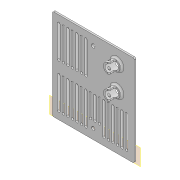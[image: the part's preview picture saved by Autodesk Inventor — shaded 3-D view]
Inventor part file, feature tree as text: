
AUTODESK INVENTOR PART (.ipt)
format: ipt  version: 2020 (Build 240168000, 168)  size: 380,928 bytes
history: native  units: mm
features: other x9, extrude x4, sketch x4, fillet x2
ambient origin geometry x8: Origin, YZ Plane, XZ Plane, XY Plane, X Axis, Y Axis, Z Axis, Center Point
bodies: Body1 (feature_tree)
feature tree (19):
  other  "Sólido1"
  other  "Plano de trabalho1"
  extrude  "Extrusão1"  Depth=0.5mm
  extrude  "Extrusão2"  Depth=1.0mm
  fillet  "Arredondamento1"  Radius=0.5mm
  extrude  "Extrusão3"  Depth=4.5mm
  extrude  "Extrusão4"  Depth=2.0mm
  fillet  "Arredondamento2"  Radius=10.0mm
  sketch  "Esboço1"  dims[d0=0.5mm d1=0.5mm]
  other  "Referência1"
  other  "Referência2"
  sketch  "Esboço2"  dims[d2=1.0mm d3=1.0mm d4=0.5mm]
  sketch  "Esboço3"  dims[d5=0.5mm d6=4.5mm]
  other  "Contorno projetado1"
  other  "Contorno projetado2"
  sketch  "Esboço4"  dims[d7=0.5mm d8=4.5mm d9=10.0mm d10=10.0mm d11=18.0mm d12=23.0mm d13=23.0mm d14=31.0mm d15=42.0mm d16=42.0mm d17=31.0mm d18=31.0mm d19=3.2mm d20=3.2mm d21=70.0mm d23=6.0mm d24=10.0mm d26=10.0mm d28=2.2mm d29=0.0mm d30=3.2mm d31=6.0mm d32=30.0mm d34=6.0mm d35=10.0mm d37=10.0mm d39=3.2mm d40=6.0mm d41=50.0mm d43=6.0mm d44=10.0mm d46=10.0mm d48=20.0mm d50=6.0mm d51=10.0mm d53=10.0mm d55=14.0mm d56=14.0mm d57=3.0mm d58=0.0mm d59=2.2mm d60=8.0mm d61=0.0mm d62=3.0mm d63=100.0mm d64=0.0mm d65=2.0mm]
  other  "Calorímetro.iam"
  other  "suporte_fechamento:2"
  other  "suporte_fechamento:3"
